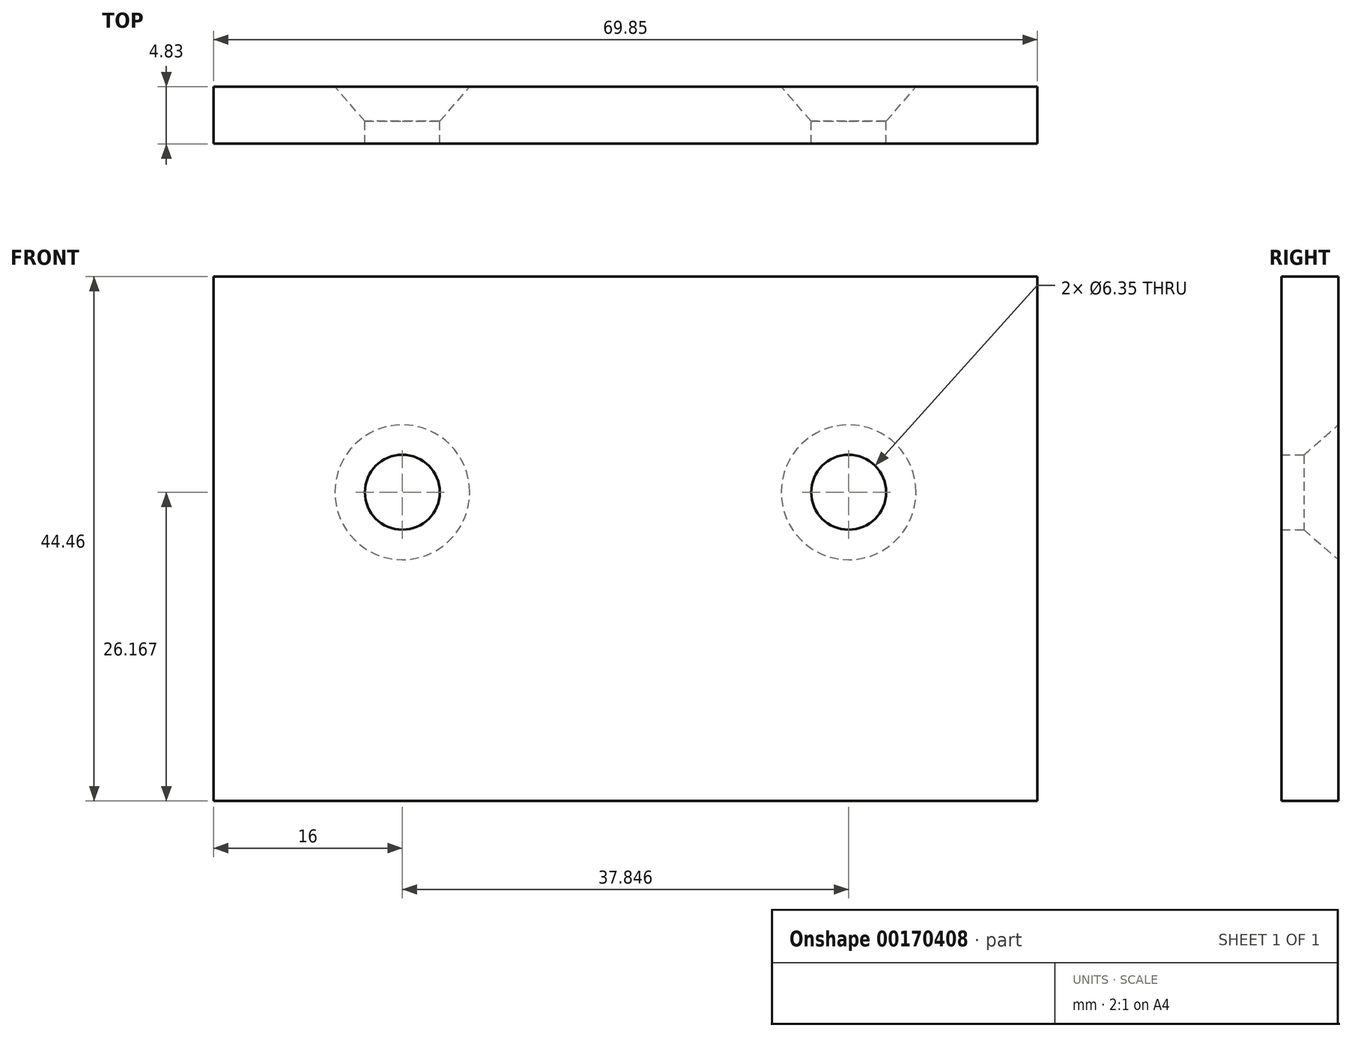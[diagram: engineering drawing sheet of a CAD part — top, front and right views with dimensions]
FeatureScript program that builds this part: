
annotation { "Feature Type Name" : "Feature", "Feature Type Description" : "" }
export const myFeature = defineFeature(function(context is Context, id is Id, definition is map)
    precondition{}
    {
        {
            var Q0;
            Q0=qCreatedBy(makeId("Front.planeOp"),FACE);
            var sketch = newSketch(context, id + "F0", { "sketchPlane" : qUnion([Q0])});
            skLineSegment(sketch, "E0.bottom", {"start": v(-35.05, 22.23) * mm, "end": v(34.8, 22.23) * mm});
            skLineSegment(sketch, "E0.top", {"start": v(-35.05, -22.23) * mm, "end": v(34.8, -22.23) * mm});
            skLineSegment(sketch, "E0.left", {"start": v(-35.05, 22.22) * mm, "end": v(-35.05, -22.23) * mm});
            skLineSegment(sketch, "E0.right", {"start": v(34.8, 22.23) * mm, "end": v(34.8, -22.23) * mm});
            skPoint(sketch, "E1", {"position": v(-19.05, 3.94) * mm});
            skPoint(sketch, "E2", {"position": v(18.8, 3.94) * mm});
            skSolve(sketch);
        }
        {
            var Q0;
            Q0=makeQuery(id+"F0.imprint","IMPRINT",FACE,{"disambiguationData":[TD([[makeQuery(id+"F0.imprint","IMPRINT",EDGE,{"derivedFrom":sQuery(id+"F0.wireOp",EDGE,"E0.bottom")}),-1.0]])]});
            extrude(context, id + "F1", {"entities" : qUnion([Q0]), "depth" : 4.83 * mm});
        }
        {
            var Q0;
            Q0=sQuery(id+"F0.wireOp",VERTEX,"E1");
            var Q1;
            Q1=sQuery(id+"F0.wireOp",VERTEX,"E2");
            var Q2;
            Q2=makeQuery(id+"F1.opExtrude","SWEPT_BODY",BODY,{"disambiguationData":[OSD([sQuery(id+"F0.wireOp",EDGE,"E0.bottom"),sQuery(id+"F0.wireOp",EDGE,"E0.top"),sQuery(id+"F0.wireOp",EDGE,"E0.left"),sQuery(id+"F0.wireOp",EDGE,"E0.right")])]});
            hole(context, id + "F2", {"style" : HoleStyle.C_SINK, "endStyle" : HoleEndStyle.THROUGH, "oppositeDirection" : true, "holeDiameter" : 6.35 * mm, "cSinkDiameter" : 11.43 * mm, "cSinkAngle" : 82 * degree, "startFromSketch" : true, "locations" : qUnion([Q0, Q1]), "scope" : qUnion([Q2]), "isTappedThrough" : true});
        }
    });
